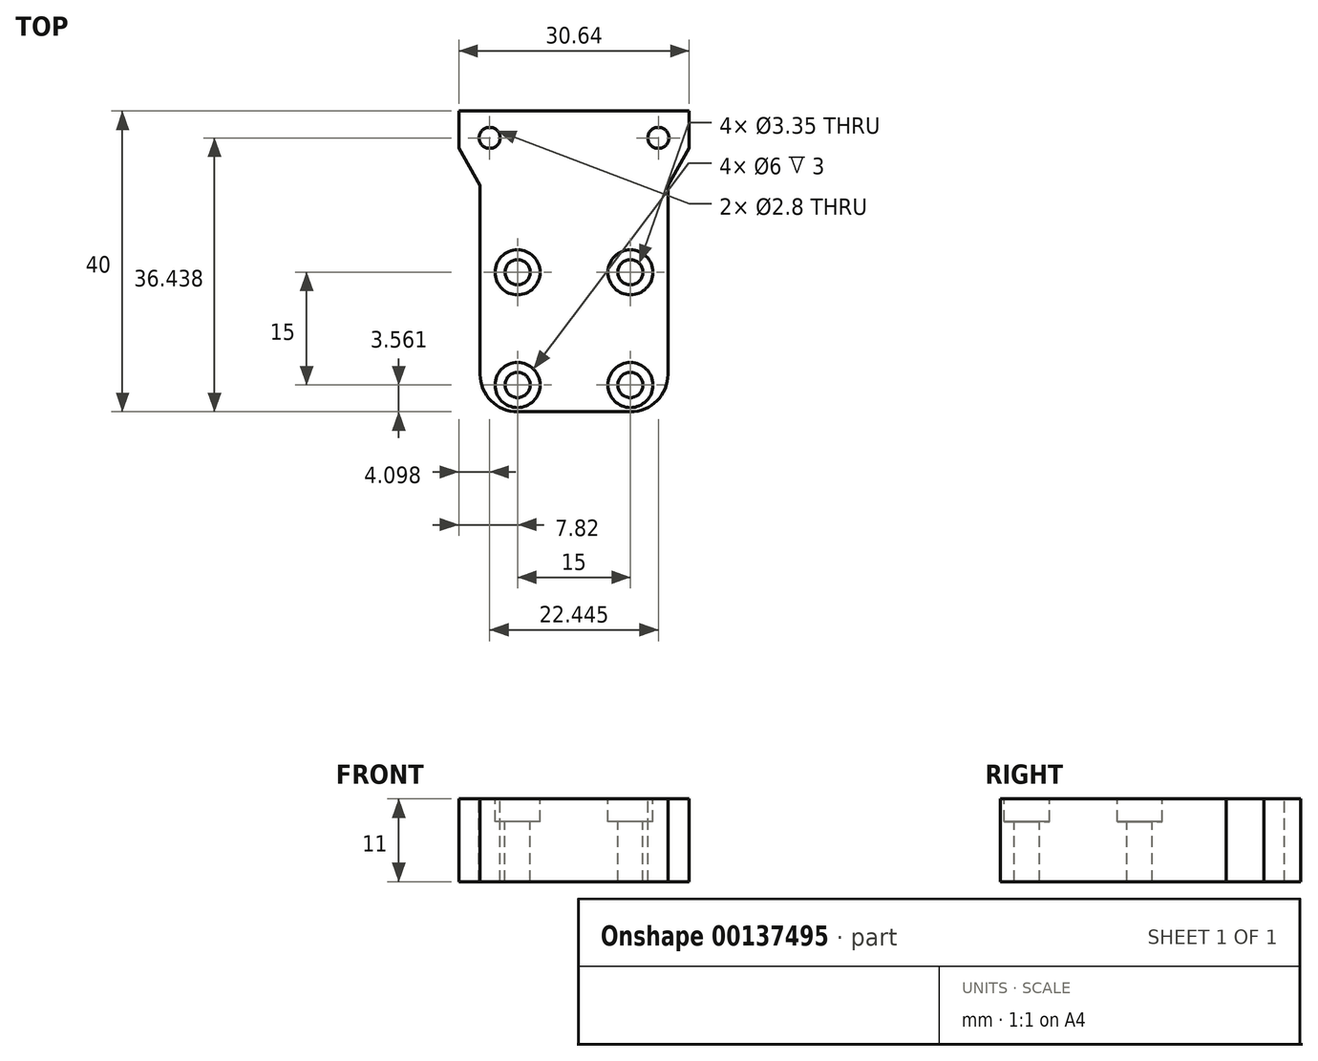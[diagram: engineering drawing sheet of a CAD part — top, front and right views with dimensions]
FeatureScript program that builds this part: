
annotation { "Feature Type Name" : "Feature", "Feature Type Description" : "" }
export const myFeature = defineFeature(function(context is Context, id is Id, definition is map)
    precondition{}
    {
        {
            var Q0;
            Q0=qCreatedBy(makeId("Top.planeOp"),FACE);
            var sketch = newSketch(context, id + "F0", { "sketchPlane" : qUnion([Q0])});
            skLineSegment(sketch, "E0.bottom", {"start": v(0, 0) * mm, "end": v(25, 0) * mm});
            skLineSegment(sketch, "E0.top", {"start": v(-2.82, 40) * mm, "end": v(27.82, 40) * mm});
            skLineSegment(sketch, "E1", {"start": v(0, 30.1) * mm, "end": v(25, 30.1) * mm});
            skLineSegment(sketch, "E2", {"start": v(-2.82, 35.1) * mm, "end": v(27.82, 35.1) * mm});
            skLineSegment(sketch, "E3", {"start": v(0, 0) * mm, "end": v(0, 30.1) * mm});
            skLineSegment(sketch, "E4", {"start": v(0, 30.1) * mm, "end": v(-2.82, 35.1) * mm});
            skLineSegment(sketch, "E5", {"start": v(-2.82, 35.1) * mm, "end": v(-2.82, 40) * mm});
            skLineSegment(sketch, "E6", {"start": v(25, 0) * mm, "end": v(25, 30.1) * mm});
            skLineSegment(sketch, "E7", {"start": v(25, 30.1) * mm, "end": v(27.82, 35.1) * mm});
            skLineSegment(sketch, "E8", {"start": v(27.82, 35.1) * mm, "end": v(27.82, 40) * mm});
            skSolve(sketch);
        }
        {
            var Q0;
            Q0=qSketchRegion(id+"F0",true);
            extrude(context, id + "F1", {"entities" : qUnion([Q0]), "depth" : 11 * mm});
        }
        {
            var Q0;
            Q0=makeQuery(id+"F1.opExtrude","CAP_FACE",FACE,{"disambiguationData":[OSD([sQuery(id+"F0.wireOp",EDGE,"E0.bottom"),sQuery(id+"F0.wireOp",EDGE,"E0.top"),sQuery(id+"F0.wireOp",EDGE,"E3"),sQuery(id+"F0.wireOp",EDGE,"E4"),sQuery(id+"F0.wireOp",EDGE,"E5"),sQuery(id+"F0.wireOp",EDGE,"E6"),sQuery(id+"F0.wireOp",EDGE,"E7"),sQuery(id+"F0.wireOp",EDGE,"E8")])],"isStart":false});
            var sketch = newSketch(context, id + "F2", { "sketchPlane" : qUnion([Q0])});
            skCircle(sketch, "E9", {"center": v(5, 18.56) * mm, "radius": 1.68 * mm});
            skCircle(sketch, "E10", {"center": v(20, 18.56) * mm, "radius": 1.68 * mm});
            skCircle(sketch, "E11", {"center": v(5, 3.56) * mm, "radius": 1.68 * mm});
            skCircle(sketch, "E12", {"center": v(20, 3.56) * mm, "radius": 1.68 * mm});
            skLineSegment(sketch, "E13", {"start": v(5, 18.56) * mm, "end": v(0, 18.56) * mm});
            skLineSegment(sketch, "E14", {"start": v(20, 3.56) * mm, "end": v(25, 3.56) * mm});
            skCircle(sketch, "E15", {"center": v(5, 18.56) * mm, "radius": 3 * mm});
            skCircle(sketch, "E16", {"center": v(20, 18.56) * mm, "radius": 3 * mm});
            skCircle(sketch, "E17", {"center": v(5, 3.56) * mm, "radius": 3 * mm});
            skCircle(sketch, "E18", {"center": v(20, 3.56) * mm, "radius": 3 * mm});
            skSolve(sketch);
        }
        {
            var Q0;
            Q0=makeQuery(id+"F2.imprint","IMPRINT",FACE,{"disambiguationData":[TD([[makeQuery(id+"F2.imprint","IMPRINT",EDGE,{"derivedFrom":sQuery(id+"F2.wireOp",EDGE,"E9")}),1.0]])]});
            var Q1;
            Q1=makeQuery(id+"F2.imprint","IMPRINT",FACE,{"disambiguationData":[TD([[makeQuery(id+"F2.imprint","IMPRINT",EDGE,{"derivedFrom":sQuery(id+"F2.wireOp",EDGE,"E10")}),1.0]])]});
            var Q2;
            Q2=makeQuery(id+"F2.imprint","IMPRINT",FACE,{"disambiguationData":[TD([[makeQuery(id+"F2.imprint","IMPRINT",EDGE,{"derivedFrom":sQuery(id+"F2.wireOp",EDGE,"E12")}),1.0]])]});
            var Q3;
            Q3=makeQuery(id+"F2.imprint","IMPRINT",FACE,{"disambiguationData":[TD([[makeQuery(id+"F2.imprint","IMPRINT",EDGE,{"derivedFrom":sQuery(id+"F2.wireOp",EDGE,"E11")}),1.0]])]});
            var Q4;
            Q4=makeQuery(id+"F2.imprint","IMPRINT",FACE,{"disambiguationData":[TD([[makeQuery(id+"F2.imprint","IMPRINT",EDGE,{"derivedFrom":sQuery(id+"F2.wireOp",EDGE,"97d24b09-4827-4c46-a1fd-a3ea8677536d")}),1.0]])]});
            var Q5;
            Q5=makeQuery(id+"F2.imprint","IMPRINT",FACE,{"disambiguationData":[TD([[makeQuery(id+"F2.imprint","IMPRINT",EDGE,{"derivedFrom":sQuery(id+"F2.wireOp",EDGE,"b6eb7b6f-8bb0-4363-9520-a6d7085f5256")}),1.0]])]});
            extrude(context, id + "F3", {"entities" : qUnion([Q0, Q1, Q2, Q3, Q4, Q5]), "operationType" : NewBodyOperationType.REMOVE, "oppositeDirection" : true, "depth" : 25 * mm});
        }
        {
            var Q0;
            Q0=makeQuery(id+"F1.opExtrude","SWEPT_EDGE",EDGE,{"disambiguationData":[OSD([sQuery(id+"F0.wireOp",EDGE,"E0.bottom"),sQuery(id+"F0.wireOp",EDGE,"E0.left")])]});
            var Q1;
            Q1=makeQuery(id+"F1.opExtrude","SWEPT_EDGE",EDGE,{"disambiguationData":[OSD([sQuery(id+"F0.wireOp",EDGE,"E0.bottom"),sQuery(id+"F0.wireOp",EDGE,"E0.right")])]});
            fillet(context, id + "F4", {"entities" : qUnion([Q0, Q1]), "radius" : 5 * mm, "tangentPropagation" : true, "allowEdgeOverflow" : false});
        }
        {
            var Q0;
            Q0=makeQuery(id+"F0.imprint","IMPRINT",FACE,{"disambiguationData":[TD([[makeQuery(id+"F0.imprint","IMPRINT",EDGE,{"derivedFrom":sQuery(id+"F0.wireOp",EDGE,"E0.top")}),-1.0]])]});
            var Q1;
            Q1=makeQuery(id+"F0.imprint","IMPRINT",FACE,{"disambiguationData":[TD([[makeQuery(id+"F0.imprint","IMPRINT",EDGE,{"derivedFrom":sQuery(id+"F0.wireOp",EDGE,"E1")}),1.0]])]});
            extrude(context, id + "F5", {"entities" : qUnion([Q0, Q1]), "operationType" : NewBodyOperationType.ADD, "depth" : 11 * mm});
        }
        {
            var Q0;
            Q0=makeQuery(id+"F1.opExtrude","CAP_FACE",FACE,{"disambiguationData":[OSD([sQuery(id+"F0.wireOp",EDGE,"E0.bottom"),sQuery(id+"F0.wireOp",EDGE,"E0.top"),sQuery(id+"F0.wireOp",EDGE,"E3"),sQuery(id+"F0.wireOp",EDGE,"E4"),sQuery(id+"F0.wireOp",EDGE,"E5"),sQuery(id+"F0.wireOp",EDGE,"E6"),sQuery(id+"F0.wireOp",EDGE,"E7"),sQuery(id+"F0.wireOp",EDGE,"E8")])],"isStart":false});
            var sketch = newSketch(context, id + "F6", { "sketchPlane" : qUnion([Q0])});
            skCircle(sketch, "E19", {"center": v(23.72, 36.44) * mm, "radius": 1.4 * mm});
            skCircle(sketch, "E20", {"center": v(1.28, 36.44) * mm, "radius": 1.4 * mm});
            skLineSegment(sketch, "E21", {"start": v(1.28, 36.44) * mm, "end": v(-2.82, 36.44) * mm});
            skLineSegment(sketch, "E22", {"start": v(23.72, 36.44) * mm, "end": v(27.82, 36.44) * mm});
            skSolve(sketch);
        }
        {
            var Q0;
            Q0=qSketchRegion(id+"F6",true);
            extrude(context, id + "F7", {"entities" : qUnion([Q0]), "operationType" : NewBodyOperationType.REMOVE, "endBound" : BoundingType.THROUGH_ALL, "oppositeDirection" : true, "depth" : 25 * mm});
        }
        {
            var Q0;
            Q0=makeQuery(id+"F2.imprint","IMPRINT",FACE,{"disambiguationData":[TD([[makeQuery(id+"F2.imprint","IMPRINT",EDGE,{"derivedFrom":sQuery(id+"F2.wireOp",EDGE,"E9")}),-1.0]])]});
            var Q1;
            Q1=makeQuery(id+"F2.imprint","IMPRINT",FACE,{"disambiguationData":[TD([[makeQuery(id+"F2.imprint","IMPRINT",EDGE,{"derivedFrom":sQuery(id+"F2.wireOp",EDGE,"E11")}),-1.0]])]});
            var Q2;
            Q2=makeQuery(id+"F2.imprint","IMPRINT",FACE,{"disambiguationData":[TD([[makeQuery(id+"F2.imprint","IMPRINT",EDGE,{"derivedFrom":sQuery(id+"F2.wireOp",EDGE,"E10")}),-1.0]])]});
            var Q3;
            Q3=makeQuery(id+"F2.imprint","IMPRINT",FACE,{"disambiguationData":[TD([[makeQuery(id+"F2.imprint","IMPRINT",EDGE,{"derivedFrom":sQuery(id+"F2.wireOp",EDGE,"E12")}),-1.0]])]});
            extrude(context, id + "F8", {"entities" : qUnion([Q0, Q1, Q2, Q3]), "operationType" : NewBodyOperationType.REMOVE, "oppositeDirection" : true, "depth" : 3 * mm});
        }
    });
